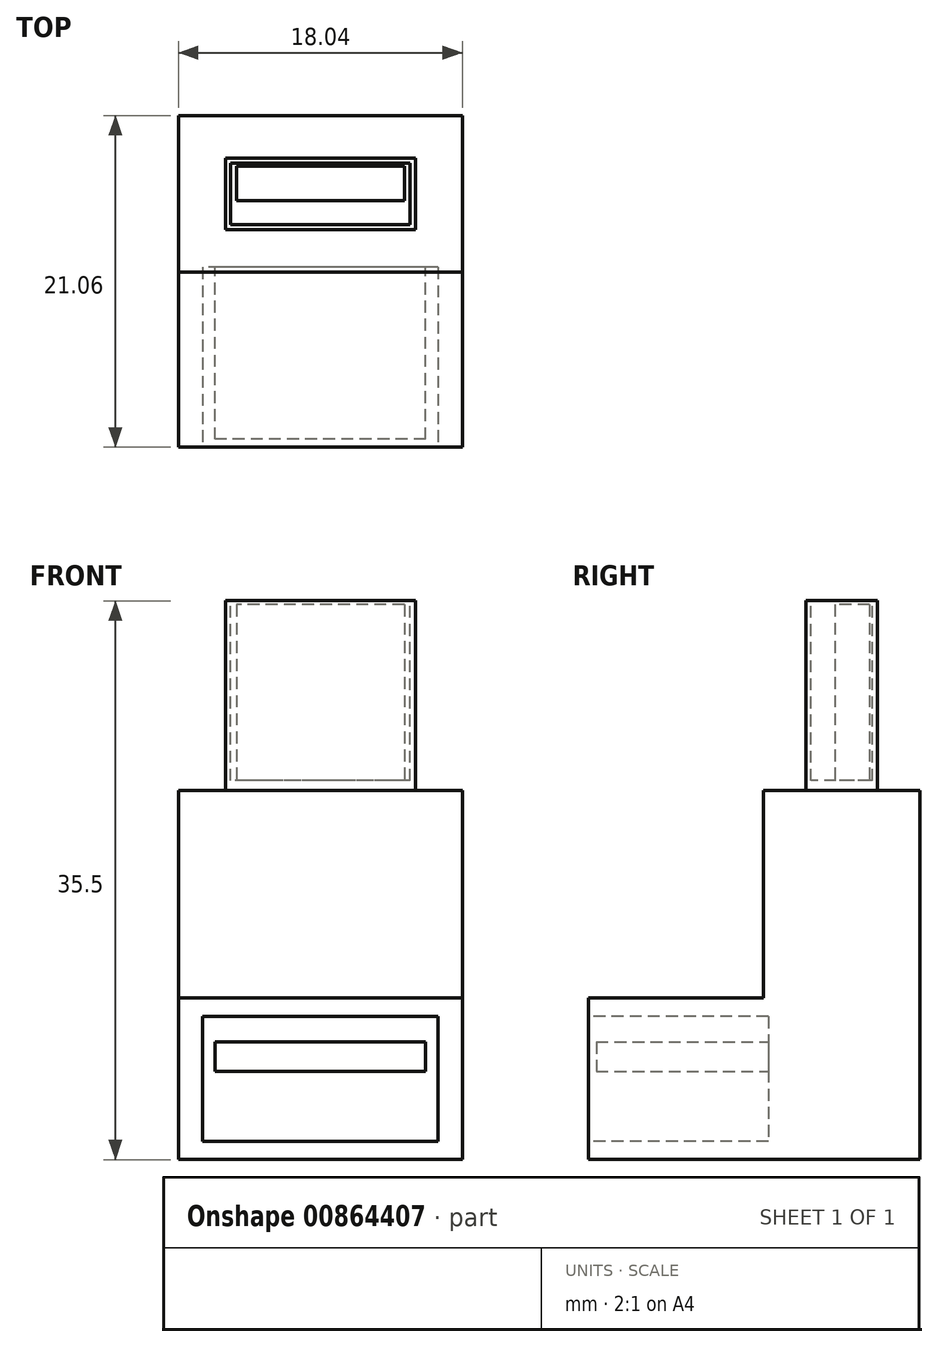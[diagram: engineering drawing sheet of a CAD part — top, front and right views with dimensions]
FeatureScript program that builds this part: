
annotation { "Feature Type Name" : "Feature", "Feature Type Description" : "" }
export const myFeature = defineFeature(function(context is Context, id is Id, definition is map)
    precondition{}
    {
        {
            var Q0;
            Q0=qCreatedBy(makeId("Front.planeOp"),FACE);
            var sketch = newSketch(context, id + "F0", { "sketchPlane" : qUnion([Q0])});
            skLineSegment(sketch, "E0.bottom", {"start": v(9.02, 11.72) * mm, "end": v(-9.02, 11.72) * mm});
            skLineSegment(sketch, "E0.top", {"start": v(9.02, -11.72) * mm, "end": v(-9.02, -11.72) * mm});
            skLineSegment(sketch, "E0.left", {"start": v(9.02, 11.72) * mm, "end": v(9.02, -11.72) * mm});
            skLineSegment(sketch, "E0.right", {"start": v(-9.02, 11.72) * mm, "end": v(-9.02, -11.72) * mm});
            skPoint(sketch, "E0.middle", {"position": v(0, 0) * mm});
            skSolve(sketch);
        }
        {
            var Q0;
            Q0 = qSketchRegion(id + "F0", true);
            extrude(context, id + "F1", {"entities" : qUnion([Q0]), "depth" : 21.06 * mm, "offsetDistance" : 25.4 * mm});
        }
        {
            var Q0;
            Q0=makeQuery(id+"F1.opExtrude","SWEPT_FACE",FACE,{"disambiguationData":[OSD([sQuery(id+"F0.wireOp",EDGE,"E0.bottom")])]});
            var sketch = newSketch(context, id + "F2", { "sketchPlane" : qUnion([Q0])});
            skLineSegment(sketch, "E1.bottom", {"start": v(-9.02, 0) * mm, "end": v(9.02, 0) * mm});
            skLineSegment(sketch, "E1.top", {"start": v(-9.02, -9.93) * mm, "end": v(9.02, -9.93) * mm});
            skLineSegment(sketch, "E1.left", {"start": v(-9.02, 0) * mm, "end": v(-9.02, -9.93) * mm});
            skLineSegment(sketch, "E1.right", {"start": v(9.02, 0) * mm, "end": v(9.02, -9.93) * mm});
            skLineSegment(sketch, "E2.top", {"start": v(-9.02, -21.06) * mm, "end": v(9.02, -21.06) * mm});
            skLineSegment(sketch, "E2.left", {"start": v(-9.02, -9.93) * mm, "end": v(-9.02, -21.06) * mm});
            skLineSegment(sketch, "E2.right", {"start": v(9.02, -9.93) * mm, "end": v(9.02, -21.06) * mm});
            skSolve(sketch);
        }
        {
            var Q0;
            Q0=makeQuery(id+"F2.imprint","IMPRINT",FACE,{"disambiguationData":[TD([[makeQuery(id+"F2.imprint","IMPRINT",EDGE,{"derivedFrom":sQuery(id+"F2.wireOp",EDGE,"E1.top")}),-1.0]])]});
            extrude(context, id + "F3", {"entities" : qUnion([Q0]), "operationType" : NewBodyOperationType.REMOVE, "oppositeDirection" : true, "depth" : 13.17 * mm, "offsetDistance" : 25.4 * mm});
        }
        {
            var Q0;
            Q0=makeQuery(id+"F1.opExtrude","SWEPT_FACE",FACE,{"disambiguationData":[OSD([sQuery(id+"F0.wireOp",EDGE,"E0.bottom")])]});
            var sketch = newSketch(context, id + "F4", { "sketchPlane" : qUnion([Q0])});
            skLineSegment(sketch, "E3.bottom", {"start": v(6.03, -2.7) * mm, "end": v(-6.03, -2.7) * mm});
            skLineSegment(sketch, "E3.top", {"start": v(6.03, -7.23) * mm, "end": v(-6.03, -7.23) * mm});
            skLineSegment(sketch, "E3.left", {"start": v(6.03, -2.7) * mm, "end": v(6.03, -7.23) * mm});
            skLineSegment(sketch, "E3.right", {"start": v(-6.03, -2.7) * mm, "end": v(-6.03, -7.23) * mm});
            skPoint(sketch, "E3.middle", {"position": v(0, -4.97) * mm});
            skPoint(sketch, "E3.middle.positionSnap0", {"position": v(-9.02, -4.97) * mm});
            skPoint(sketch, "E3.centerSnap0", {"position": v(-9.02, -4.97) * mm});
            skSolve(sketch);
        }
        {
            var Q0;
            Q0 = qSketchRegion(id + "F4", true);
            extrude(context, id + "F5", {"entities" : qUnion([Q0]), "operationType" : NewBodyOperationType.ADD, "depth" : 12.06 * mm, "offsetDistance" : 25.4 * mm});
        }
        {
            var Q0;
            Q0=makeQuery(id+"F1.opExtrude","CAP_FACE",FACE,{"disambiguationData":[OSD([sQuery(id+"F0.wireOp",EDGE,"E0.bottom"),sQuery(id+"F0.wireOp",EDGE,"E0.top"),sQuery(id+"F0.wireOp",EDGE,"E0.left"),sQuery(id+"F0.wireOp",EDGE,"E0.right")])],"isStart":false});
            var sketch = newSketch(context, id + "F6", { "sketchPlane" : qUnion([Q0])});
            skLineSegment(sketch, "E4.bottom", {"start": v(7.47, -2.62) * mm, "end": v(-7.47, -2.62) * mm});
            skLineSegment(sketch, "E4.top", {"start": v(7.47, -10.55) * mm, "end": v(-7.47, -10.55) * mm});
            skLineSegment(sketch, "E4.left", {"start": v(7.47, -2.62) * mm, "end": v(7.47, -10.55) * mm});
            skLineSegment(sketch, "E4.right", {"start": v(-7.47, -2.62) * mm, "end": v(-7.47, -10.55) * mm});
            skPoint(sketch, "E4.middle", {"position": v(0, -6.58) * mm});
            skPoint(sketch, "E4.middle.positionSnap0", {"position": v(9.02, -6.58) * mm});
            skPoint(sketch, "E4.middle.positionSnap1", {"position": v(0, -1.45) * mm});
            skPoint(sketch, "E4.centerSnap0", {"position": v(9.02, -6.58) * mm});
            skPoint(sketch, "E4.centerSnap1", {"position": v(0, -1.45) * mm});
            skSolve(sketch);
        }
        {
            var Q0;
            Q0 = qSketchRegion(id + "F6", true);
            extrude(context, id + "F7", {"entities" : qUnion([Q0]), "operationType" : NewBodyOperationType.REMOVE, "oppositeDirection" : true, "depth" : 11.43 * mm, "offsetDistance" : 25.4 * mm});
        }
        {
            var Q0;
            Q0=makeQuery(id+"F5.opExtrude","CAP_FACE",FACE,{"disambiguationData":[OSD([sQuery(id+"F4.wireOp",EDGE,"E3.bottom"),sQuery(id+"F4.wireOp",EDGE,"E3.top"),sQuery(id+"F4.wireOp",EDGE,"E3.left"),sQuery(id+"F4.wireOp",EDGE,"E3.right")])],"isStart":false});
            var sketch = newSketch(context, id + "F8", { "sketchPlane" : qUnion([Q0])});
            skLineSegment(sketch, "E5.bottom", {"start": v(5.69, -3.02) * mm, "end": v(-5.69, -3.02) * mm});
            skLineSegment(sketch, "E5.top", {"start": v(5.69, -6.9) * mm, "end": v(-5.69, -6.9) * mm});
            skLineSegment(sketch, "E5.left", {"start": v(5.69, -3.02) * mm, "end": v(5.69, -6.9) * mm});
            skLineSegment(sketch, "E5.right", {"start": v(-5.69, -3.02) * mm, "end": v(-5.69, -6.9) * mm});
            skPoint(sketch, "E5.middle", {"position": v(0, -4.97) * mm});
            skPoint(sketch, "E5.middle.positionSnap0", {"position": v(6.03, -4.97) * mm});
            skPoint(sketch, "E5.middle.positionSnap1", {"position": v(0, -2.7) * mm});
            skPoint(sketch, "E5.centerSnap0", {"position": v(6.03, -4.97) * mm});
            skPoint(sketch, "E5.centerSnap1", {"position": v(0, -2.7) * mm});
            skSolve(sketch);
        }
        {
            var Q0;
            Q0 = qSketchRegion(id + "F8", true);
            extrude(context, id + "F9", {"entities" : qUnion([Q0]), "operationType" : NewBodyOperationType.REMOVE, "oppositeDirection" : true, "depth" : 11.43 * mm, "offsetDistance" : 25.4 * mm});
        }
        {
            var Q0;
            Q0=makeQuery(id+"F9.boolean.opBoolean","COPY",FACE,{"derivedFrom":makeQuery(id+"F9.opExtrude","CAP_FACE",FACE,{"disambiguationData":[OSD([sQuery(id+"F8.wireOp",EDGE,"E5.bottom"),sQuery(id+"F8.wireOp",EDGE,"E5.top"),sQuery(id+"F8.wireOp",EDGE,"E5.left"),sQuery(id+"F8.wireOp",EDGE,"E5.right")])],"isStart":false})});
            var sketch = newSketch(context, id + "F10", { "sketchPlane" : qUnion([Q0])});
            skLineSegment(sketch, "E6.bottom", {"start": v(5.34, -3.2) * mm, "end": v(-5.34, -3.2) * mm});
            skLineSegment(sketch, "E6.top", {"start": v(5.34, -5.4) * mm, "end": v(-5.34, -5.4) * mm});
            skLineSegment(sketch, "E6.left", {"start": v(5.34, -3.2) * mm, "end": v(5.34, -5.4) * mm});
            skLineSegment(sketch, "E6.right", {"start": v(-5.34, -3.2) * mm, "end": v(-5.34, -5.4) * mm});
            skPoint(sketch, "E6.middle", {"position": v(0, -4.3) * mm});
            skPoint(sketch, "E6.middle.positionSnap0", {"position": v(0, -3.02) * mm});
            skPoint(sketch, "E6.centerSnap0", {"position": v(0, -3.02) * mm});
            skSolve(sketch);
        }
        {
            var Q0;
            Q0 = qSketchRegion(id + "F10", true);
            extrude(context, id + "F11", {"entities" : qUnion([Q0]), "operationType" : NewBodyOperationType.ADD, "depth" : 11.18 * mm, "offsetDistance" : 25.4 * mm});
        }
        {
            var Q0;
            Q0=makeQuery(id+"F7.boolean.opBoolean","COPY",FACE,{"derivedFrom":makeQuery(id+"F7.opExtrude","CAP_FACE",FACE,{"disambiguationData":[OSD([sQuery(id+"F6.wireOp",EDGE,"E4.bottom"),sQuery(id+"F6.wireOp",EDGE,"E4.top"),sQuery(id+"F6.wireOp",EDGE,"E4.left"),sQuery(id+"F6.wireOp",EDGE,"E4.right")])],"isStart":false})});
            var sketch = newSketch(context, id + "F12", { "sketchPlane" : qUnion([Q0])});
            skLineSegment(sketch, "E7.bottom", {"start": v(6.69, -4.24) * mm, "end": v(-6.69, -4.24) * mm});
            skLineSegment(sketch, "E7.top", {"start": v(6.69, -6.13) * mm, "end": v(-6.69, -6.13) * mm});
            skLineSegment(sketch, "E7.left", {"start": v(6.69, -4.24) * mm, "end": v(6.69, -6.13) * mm});
            skLineSegment(sketch, "E7.right", {"start": v(-6.69, -4.24) * mm, "end": v(-6.69, -6.13) * mm});
            skPoint(sketch, "E7.middle", {"position": v(0, -5.18) * mm});
            skPoint(sketch, "E7.middle.positionSnap0", {"position": v(0, -2.62) * mm});
            skPoint(sketch, "E7.centerSnap0", {"position": v(0, -2.62) * mm});
            skSolve(sketch);
        }
        {
            var Q0;
            Q0 = qSketchRegion(id + "F12", true);
            extrude(context, id + "F13", {"entities" : qUnion([Q0]), "operationType" : NewBodyOperationType.ADD, "depth" : 10.92 * mm, "offsetDistance" : 25.4 * mm});
        }
    });
